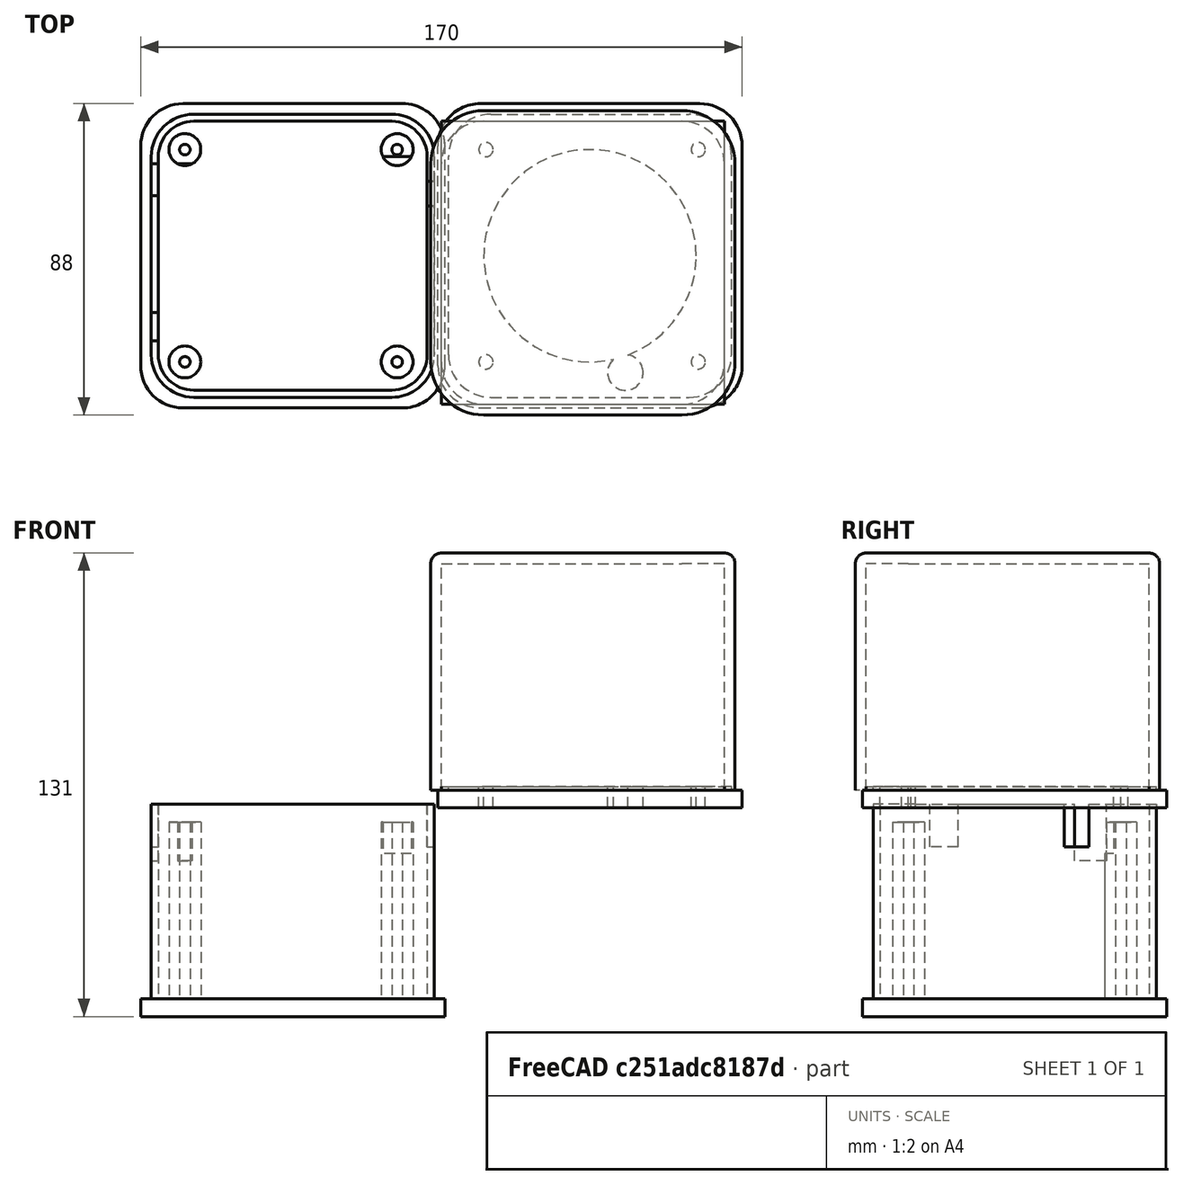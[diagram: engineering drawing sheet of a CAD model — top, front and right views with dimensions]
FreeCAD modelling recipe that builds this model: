
FCSTD DOCUMENT  (FreeCAD 0.17R13522 (Git))
Label: JoselitoBOX_V2_2
License: All rights reserved
LicenseURL: http://en.wikipedia.org/wiki/All_rights_reserved
objects: Part::Cylinder×12, Part::Box×10, Part::Cut×7, Part::MultiFuse×6, Part::Fillet×5, Part::Thickness×2
note: 42 computed .brp shape members not serialized (recipe doc carries the construction recipe); baked Part::Feature solids carry a one-line shape summary decoded from their .brp

FEATURE [Part::Box] Box002  label="Cubo002"
  AttacherType = Attacher::AttachEngine3D
  Height = 1
  Length = 80
  Width = 80
FEATURE [Part::Box] Box001  label="Cubo001"
  AttacherType = Attacher::AttachEngine3D
  Height = 64
  Length = 80
  Width = 80
FEATURE [Part::Fillet] Fillet
  Base = -> Box001
  Edges = 4 edges r=12: [Edge1,Edge3,Edge5,Edge7]
FEATURE [Part::Thickness] Thickness
  Faces = -> Fillet [Face5]
  Intersection = false
  Join = 0
  Mode = 0
  SelfIntersection = false
  Value = 3
FEATURE [Part::Box] Box  label="Cubo"
  AttacherType = Attacher::AttachEngine3D
  Height = 60
  Length = 80
  Width = 80
FEATURE [Part::Fillet] Fillet001
  Base = -> Box
  Edges = 4 edges r=12: [Edge1,Edge3,Edge5,Edge7]
FEATURE [Part::Thickness] Thickness001  label="CAJA"
  Faces = -> Fillet001 [Face5]
  Intersection = false
  Join = 0
  Mode = 0
  Placement = pos=(2,2,4) rot=(0,0,1;0rad)
  SelfIntersection = false
  Value = -2
FEATURE [Part::Cut] Cut001
  Placement = pos=(5.5,5,6) rot=(0,0,1;0rad)
FEATURE [Part::Cylinder] Cylinder002  label="Cilindro002"
  Angle = 360
  AttacherType = Attacher::AttachEngine3D
  Height = 63
  Placement = pos=(7,7,3) rot=(0,0,1;0rad)
  Radius = 1.5
FEATURE [Part::Cylinder] Cylinder003  label="Cilindro003"
  Angle = 360
  AttacherType = Attacher::AttachEngine3D
  Height = 55
  Placement = pos=(7,7,3) rot=(0,0,1;0rad)
  Radius = 4.5
FEATURE [Part::Cut] Cut002
  Base = -> Cylinder003
  Placement = pos=(5.5,65,6) rot=(0,0,1;0rad)
  Tool = -> Cylinder002
FEATURE [Part::Cylinder] Cylinder004  label="Cilindro004"
  Angle = 360
  AttacherType = Attacher::AttachEngine3D
  Height = 63
  Placement = pos=(7,7,3) rot=(0,0,1;0rad)
  Radius = 1.5
FEATURE [Part::Cylinder] Cylinder005  label="Cilindro005"
  Angle = 360
  AttacherType = Attacher::AttachEngine3D
  Height = 55
  Placement = pos=(7,7,3) rot=(0,0,1;0rad)
  Radius = 4.5
FEATURE [Part::Cut] Cut003
  Base = -> Cylinder005
  Placement = pos=(65.5,65,6) rot=(0,0,1;0rad)
  Tool = -> Cylinder004
FEATURE [Part::Cylinder] Cylinder006  label="Cilindro006"
  Angle = 360
  AttacherType = Attacher::AttachEngine3D
  Height = 63
  Placement = pos=(7,7,3) rot=(0,0,1;0rad)
  Radius = 1.5
FEATURE [Part::Cylinder] Cylinder007  label="Cilindro007"
  Angle = 360
  AttacherType = Attacher::AttachEngine3D
  Height = 55
  Placement = pos=(7,7,3) rot=(0,0,1;0rad)
  Radius = 4.5
FEATURE [Part::Cut] Cut004
  Base = -> Cylinder007
  Placement = pos=(65.5,5,6) rot=(0,0,1;0rad)
  Tool = -> Cylinder006
FEATURE [Part::MultiFuse] Fusion  label="cilindros"
  Shapes = -> [Cut001,Cut003,Cut004,Cut002]
FEATURE [Part::Box] Box003  label="Cubo003"
  AttacherType = Attacher::AttachEngine3D
  Height = 1
  Length = 80
  Width = 80
FEATURE [Part::Fillet] Fillet002
  Base = -> Box003
  Edges = 4 edges r=12: [Edge1,Edge3,Edge5,Edge7]
FEATURE [Part::Box] Box004  label="Cubo004"
  AttacherType = Attacher::AttachEngine3D
  Height = 5
  Length = 86
  Width = 86
FEATURE [Part::Fillet] Fillet003
  Base = -> Box004
  Edges = 4 edges r=12: [Edge1,Edge3,Edge5,Edge7]
  Placement = pos=(-3,-3,-5) rot=(0,0,1;0rad)
FEATURE [Part::Cylinder] Cylinder008  label="Speaker"
  Angle = 360
  AttacherType = Attacher::AttachEngine3D
  Height = 10
  Placement = pos=(42,42,-6) rot=(0,0,1;0rad)
  Radius = 30
FEATURE [Part::Cylinder] Cylinder009  label="LED"
  Angle = 360
  AttacherType = Attacher::AttachEngine3D
  Height = 10
  Placement = pos=(52,9,-6) rot=(0,0,1;0rad)
  Radius = 5
FEATURE [Part::MultiFuse] Fusion001  label="Tapa"
  Placement = pos=(2,2,0) rot=(0,0,1;0rad)
  Shapes = -> [Fillet002,Fillet003]
FEATURE [Part::Cylinder] Cylinder011  label="rod1"
  Angle = 360
  AttacherType = Attacher::AttachEngine3D
  Height = 63
  Placement = pos=(72.6,12,-9) rot=(0,0,1;0rad)
  Radius = 2
FEATURE [Part::Cylinder] Cylinder012  label="rod2"
  Angle = 360
  AttacherType = Attacher::AttachEngine3D
  Height = 63
  Placement = pos=(72.6,72,-9) rot=(0,0,1;0rad)
  Radius = 2
FEATURE [Part::Cylinder] Cylinder013  label="rod3"
  Angle = 360
  AttacherType = Attacher::AttachEngine3D
  Height = 63
  Placement = pos=(12.6,12,-9) rot=(0,0,1;0rad)
  Radius = 2
FEATURE [Part::Cylinder] Cylinder014  label="rod4"
  Angle = 360
  AttacherType = Attacher::AttachEngine3D
  Height = 63
  Placement = pos=(12.6,72,-9) rot=(0,0,1;0rad)
  Radius = 2
FEATURE [Part::Box] Box009  label="interruptor002"
  AttacherType = Attacher::AttachEngine3D
  Height = 22
  Length = 26
  Placement = pos=(62,20,-6) rot=(0,0,1;0rad)
  Width = 7
FEATURE [Part::Box] Box010  label="jackDC"
  AttacherType = Attacher::AttachEngine3D
  Height = 16
  Length = 26
  Placement = pos=(-4,15,4) rot=(0,0,1;0rad)
  Width = 9
FEATURE [Part::Box] Box011  label="jackAudio"
  AttacherType = Attacher::AttachEngine3D
  Height = 12
  Length = 26
  Placement = pos=(-4,57,4) rot=(0,0,1;0rad)
  Width = 8
FEATURE [Part::MultiFuse] Fusion002
  Placement = pos=(82,83,0) rot=(0,0,1;3.14159rad)
  Shapes = -> [Box009,Box010,Box011]
FEATURE [Part::MultiFuse] Fusion003  label="holes"
  Shapes = -> [Cylinder011,Cylinder009,Cylinder008,Cylinder012,Cylinder013,Cylinder014]
FEATURE [Part::Cut] Cut005  label="frontspeaker"
  Base = -> Fusion001
  Tool = -> Fusion003
FEATURE [Part::Box] Box012  label="Cubo005"
  AttacherType = Attacher::AttachEngine3D
  Height = 5
  Length = 86
  Width = 86
FEATURE [Part::Fillet] Fillet004
  Base = -> Box012
  Edges = 4 edges r=12: [Edge1,Edge3,Edge5,Edge7]
  Placement = pos=(-1,-1,59) rot=(0,0,1;0rad)
FEATURE [Part::MultiFuse] Fusion004
  Shapes = -> [Fusion,Thickness001]
FEATURE [Part::MultiFuse] Fusion005
  Shapes = -> [Fusion004,Fillet004]
FEATURE [Part::Cut] Cut  label="BOX_bases_holes"
  Base = -> Fusion005
  Tool = -> Fusion002
FEATURE [Part::Box] Box013  label="Cubo006"
  AttacherType = Attacher::AttachEngine3D
  Height = 10
  Length = 10
  Placement = pos=(7,60,8) rot=(0,0,1;0rad)
  Width = 10
FEATURE [Part::Cut] Cut006  label="JoselitoBox_holesV2_2"
  Base = -> Cut
  Placement = pos=(0,0,0) rot=(0,1,0;3.14159rad)
  Tool = -> Box013
